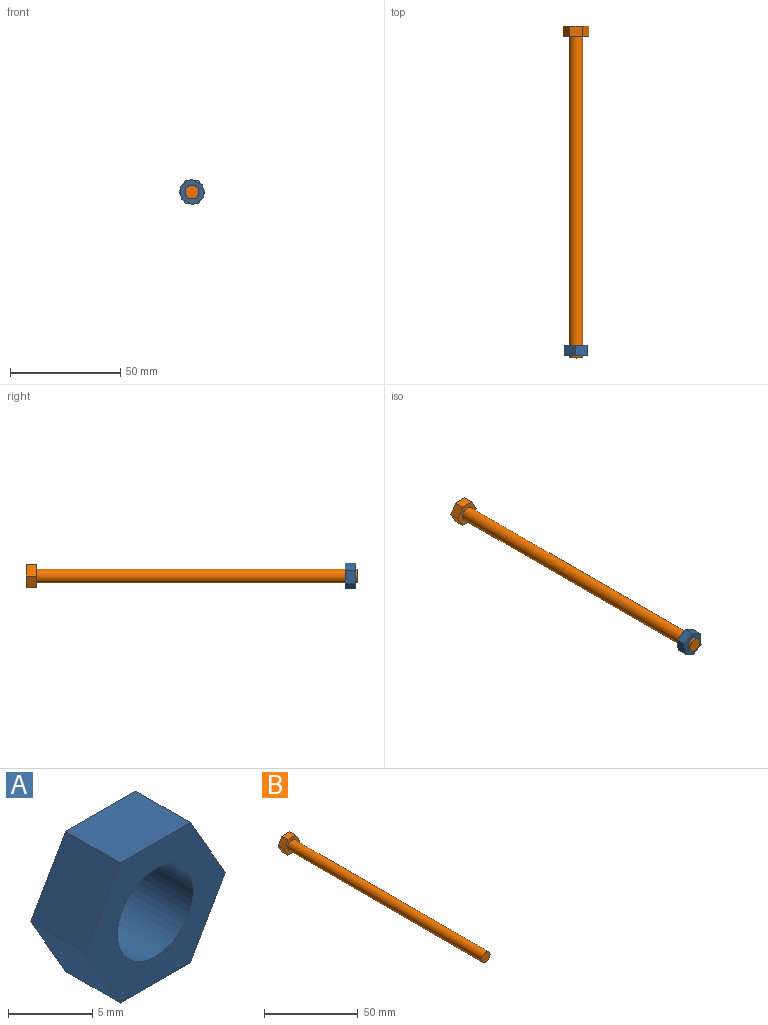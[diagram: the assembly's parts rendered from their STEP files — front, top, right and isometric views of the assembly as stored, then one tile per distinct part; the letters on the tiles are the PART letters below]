
ASSEMBLY  parts=2 mates=1
PART A: 9 faces, bbox 11.7x4.6x10.2 mm
  f0: plane 5.08x4.57mm, normal (0.87,0,0.5), area 26.8mm2, adj f1,f5,f6,f7
  f1: plane 5.87x4.57mm, normal (0,0,1), area 26.8mm2, adj f0,f2,f6,f7
  f2: plane 5.08x4.57mm, normal (-0.87,0,0.5), area 26.8mm2, adj f1,f3,f6,f7
  f3: plane 5.08x4.57mm, normal (-0.87,0,-0.5), area 26.8mm2, adj f2,f4,f6,f7
  f4: plane 5.87x4.57mm, normal (0,0,-1), area 26.8mm2, adj f3,f5,f6,f7
  f5: plane 5.08x4.57mm, normal (0.87,0,-0.5), area 26.8mm2, adj f0,f4,f6,f7
  f6: plane 11.73x10.16mm, normal (0,-1,0), area 57.7mm2, adj f0,f1,f2,f3,f4,f5,f8
  f7: plane 11.73x10.16mm, normal (0,1,0), area 57.7mm2, adj f0,f1,f2,f3,f4,f5,f8
  f8: cylinder r=3.17mm len=6.35mm, axis (0,1,0), area 91.2mm2, adj f6,f7
PART B: 10 faces, bbox 11.7x150.6x10.2 mm
  f0: cylinder r=3.17mm len=146.05mm, axis (0,-1,0), area 2913.6mm2, adj f1,f9
  f1: plane 6.35x6.35mm, normal (0,-1,0), area 31.7mm2, adj f0
  f2: plane 5.08x4.57mm, normal (-0.87,0,0.5), area 26.8mm2, adj f3,f7,f8,f9
  f3: plane 5.87x4.57mm, normal (0,0,1), area 26.8mm2, adj f2,f4,f8,f9
  f4: plane 5.08x4.57mm, normal (0.87,0,0.5), area 26.8mm2, adj f3,f5,f8,f9
  f5: plane 5.08x4.57mm, normal (0.87,0,-0.5), area 26.8mm2, adj f4,f6,f8,f9
  f6: plane 5.87x4.57mm, normal (0,0,-1), area 26.8mm2, adj f5,f7,f8,f9
  f7: plane 5.08x4.57mm, normal (-0.87,0,-0.5), area 26.8mm2, adj f2,f6,f8,f9
  f8: plane 11.73x10.16mm, normal (0,1,0), area 89.4mm2, adj f2,f3,f4,f5,f6,f7
  f9: plane 11.73x10.16mm, normal (0,-1,0), area 57.7mm2, adj f0,f2,f3,f4,f5,f6,f7
PLACE A rot(axis=(0.29,0,-0.96),180deg) t=(0,-71.76,0)mm
PLACE B at identity fixed
MATE revolute A.f8 <-> B.f0  axis (0,-1,0) through (0,-71.76,0)mm
